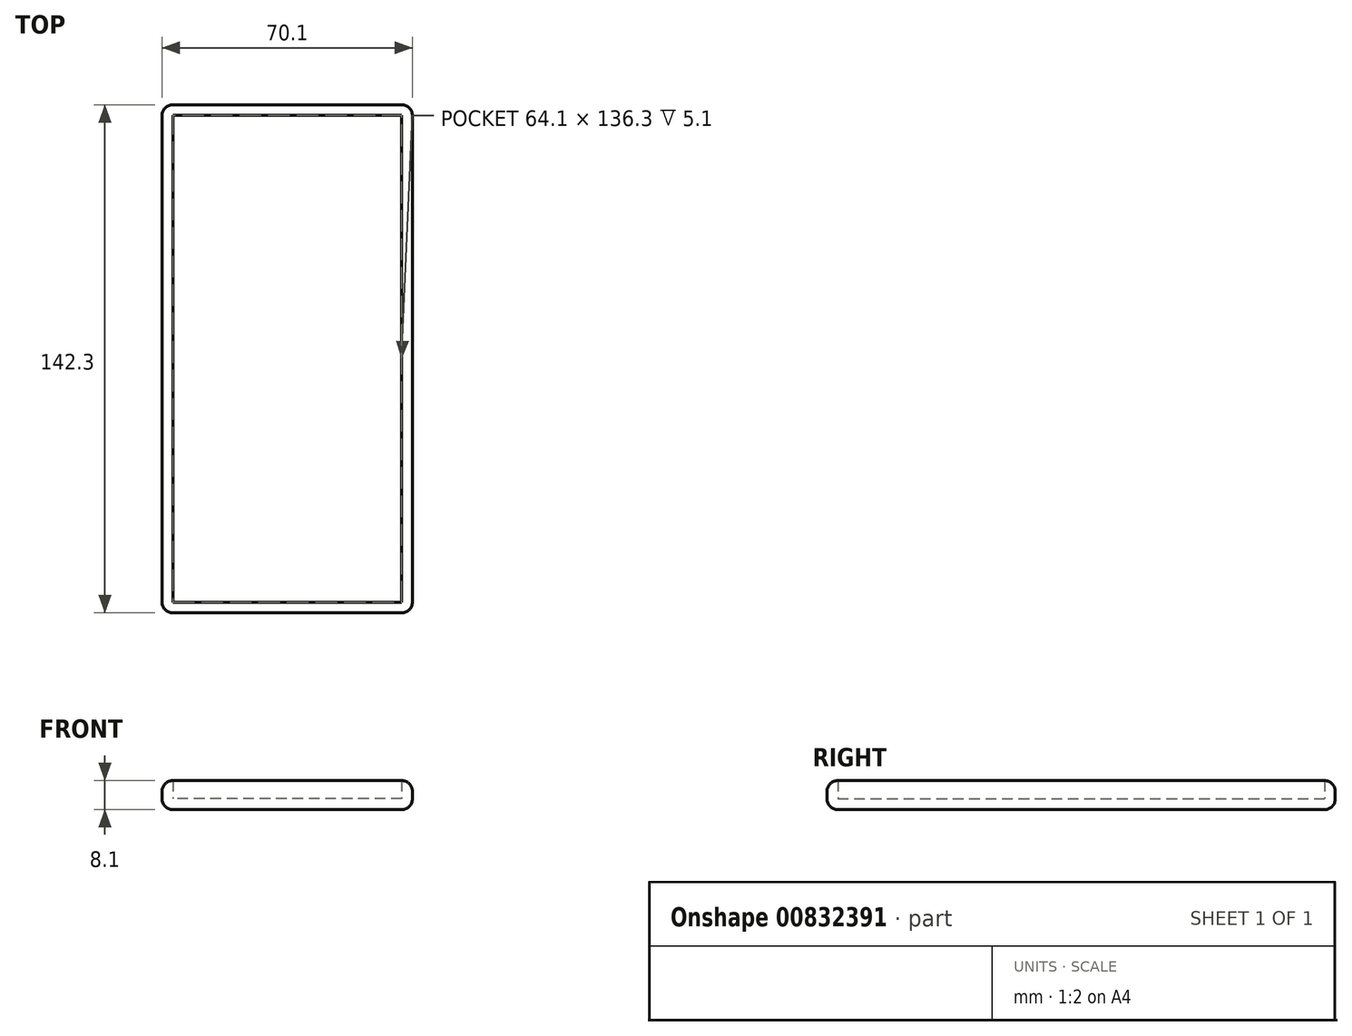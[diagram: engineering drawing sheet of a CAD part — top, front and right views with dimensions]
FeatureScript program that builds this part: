
annotation { "Feature Type Name" : "Feature", "Feature Type Description" : "" }
export const myFeature = defineFeature(function(context is Context, id is Id, definition is map)
    precondition{}
    {
        {
            var Q0;
            Q0=qCreatedBy(makeId("Top.planeOp"),FACE);
            var sketch = newSketch(context, id + "F0", { "sketchPlane" : qUnion([Q0])});
            skLineSegment(sketch, "E0.bottom", {"start": v(35.05, -71.15) * mm, "end": v(-35.05, -71.15) * mm});
            skLineSegment(sketch, "E0.top", {"start": v(35.05, 71.15) * mm, "end": v(-35.05, 71.15) * mm});
            skLineSegment(sketch, "E0.left", {"start": v(35.05, -71.15) * mm, "end": v(35.05, 71.15) * mm});
            skLineSegment(sketch, "E0.right", {"start": v(-35.05, -71.15) * mm, "end": v(-35.05, 71.15) * mm});
            skPoint(sketch, "E0.middle", {"position": v(0, 0) * mm});
            skSolve(sketch);
        }
        {
            var Q0;
            Q0 = qSketchRegion(id + "F0", true);
            extrude(context, id + "F1", {"entities" : qUnion([Q0]), "depth" : 8.1 * mm, "offsetDistance" : 25 * mm});
        }
        {
            var Q0;
            Q0=makeQuery(id+"F1.opExtrude","CAP_FACE",FACE,{"disambiguationData":[OSD([sQuery(id+"F0.wireOp",EDGE,"E0.bottom"),sQuery(id+"F0.wireOp",EDGE,"E0.top"),sQuery(id+"F0.wireOp",EDGE,"E0.left"),sQuery(id+"F0.wireOp",EDGE,"E0.right")])],"isStart":false});
            shell(context, id + "F2", {"entities" : qUnion([Q0]), "thickness" : 3 * mm});
        }
        {
            var Q0;
            Q0=makeQuery(id+"F1.opExtrude","SWEPT_FACE",FACE,{"disambiguationData":[OSD([sQuery(id+"F0.wireOp",EDGE,"E0.bottom")])]});
            var Q1;
            Q1=makeQuery(id+"F1.opExtrude","SWEPT_FACE",FACE,{"disambiguationData":[OSD([sQuery(id+"F0.wireOp",EDGE,"E0.left")])]});
            var Q2;
            Q2=makeQuery(id+"F1.opExtrude","SWEPT_FACE",FACE,{"disambiguationData":[OSD([sQuery(id+"F0.wireOp",EDGE,"E0.top")])]});
            var Q3;
            Q3=makeQuery(id+"F1.opExtrude","SWEPT_FACE",FACE,{"disambiguationData":[OSD([sQuery(id+"F0.wireOp",EDGE,"E0.right")])]});
            fillet(context, id + "F3", {"entities" : qUnion([Q0, Q1, Q2, Q3]), "radius" : 3 * mm, "tangentPropagation" : true, "allowEdgeOverflow" : false});
        }
    });
